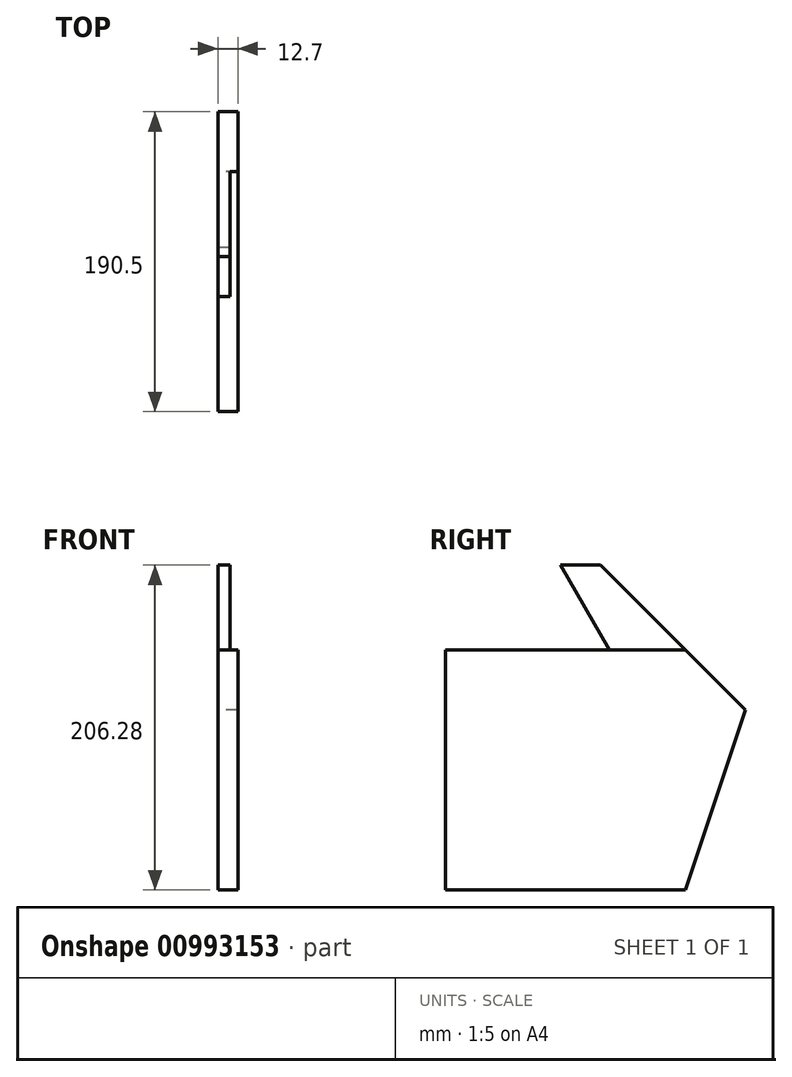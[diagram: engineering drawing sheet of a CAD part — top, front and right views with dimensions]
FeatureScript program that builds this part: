
annotation { "Feature Type Name" : "Feature", "Feature Type Description" : "" }
export const myFeature = defineFeature(function(context is Context, id is Id, definition is map)
    precondition{}
    {
        {
            var Q0;
            Q0=qCreatedBy(makeId("Right.planeOp"),FACE);
            var sketch = newSketch(context, id + "F0", { "sketchPlane" : qUnion([Q0])});
            skLineSegment(sketch, "E0.bottom", {"start": v(-23.56, 53.88) * mm, "end": v(-175.96, 53.88) * mm});
            skLineSegment(sketch, "E0.top", {"start": v(-23.56, -98.52) * mm, "end": v(-175.96, -98.52) * mm});
            skLineSegment(sketch, "E0.left", {"start": v(-23.56, 53.88) * mm, "end": v(-23.56, -98.52) * mm});
            skLineSegment(sketch, "E0.right", {"start": v(-175.96, 53.88) * mm, "end": v(-175.96, -98.52) * mm});
            skLineSegment(sketch, "E1", {"start": v(-23.56, 53.88) * mm, "end": v(-77.45, 107.76) * mm});
            skLineSegment(sketch, "E2", {"start": v(-77.45, 107.76) * mm, "end": v(-102.85, 107.76) * mm});
            skLineSegment(sketch, "E3", {"start": v(-102.85, 107.76) * mm, "end": v(-71.74, 53.88) * mm});
            skLineSegment(sketch, "E4", {"start": v(-23.56, 53.88) * mm, "end": v(14.54, 15.78) * mm});
            skLineSegment(sketch, "E5", {"start": v(14.54, 15.78) * mm, "end": v(-23.56, 15.78) * mm});
            skLineSegment(sketch, "E6", {"start": v(14.54, 15.78) * mm, "end": v(-23.56, -98.52) * mm});
            skSolve(sketch);
        }
        {
            var Q0;
            Q0=makeQuery(id+"F0.imprint","IMPRINT",FACE,{"disambiguationData":[TD([[makeQuery(id+"F0.imprint","IMPRINT",EDGE,{"derivedFrom":sQuery(id+"F0.wireOp",EDGE,"E0.top")}),-1.0]])]});
            var Q1;
            {var subQ0=sQuery(id+"F0.wireOp",EDGE,"E4");Q1=makeQuery(id+"F0.imprint","IMPRINT",FACE,{"disambiguationData":[TD([[makeQuery(id+"F0.imprint","IMPRINT",EDGE,{"derivedFrom":subQ0}),-1.0]])]});}
            var Q2;
            {var subQ2=sQuery(id+"F0.wireOp",EDGE,"E5");Q2=makeQuery(id+"F0.imprint","IMPRINT",FACE,{"disambiguationData":[TD([[makeQuery(id+"F0.imprint","IMPRINT",EDGE,{"derivedFrom":subQ2}),1.0]])]});}
            extrude(context, id + "F1", {"entities" : qUnion([Q0, Q1, Q2]), "depth" : 12.7 * mm, "offsetDistance" : 25.4 * mm});
        }
        {
            var Q0;
            {var subQ0=sQuery(id+"F0.wireOp",EDGE,"E1");Q0=makeQuery(id+"F0.imprint","IMPRINT",FACE,{"disambiguationData":[TD([[makeQuery(id+"F0.imprint","IMPRINT",EDGE,{"derivedFrom":subQ0}),1.0]])]});}
            extrude(context, id + "F2", {"entities" : qUnion([Q0]), "operationType" : NewBodyOperationType.ADD, "depth" : 7.62 * mm, "offsetDistance" : 25.4 * mm});
        }
    });
